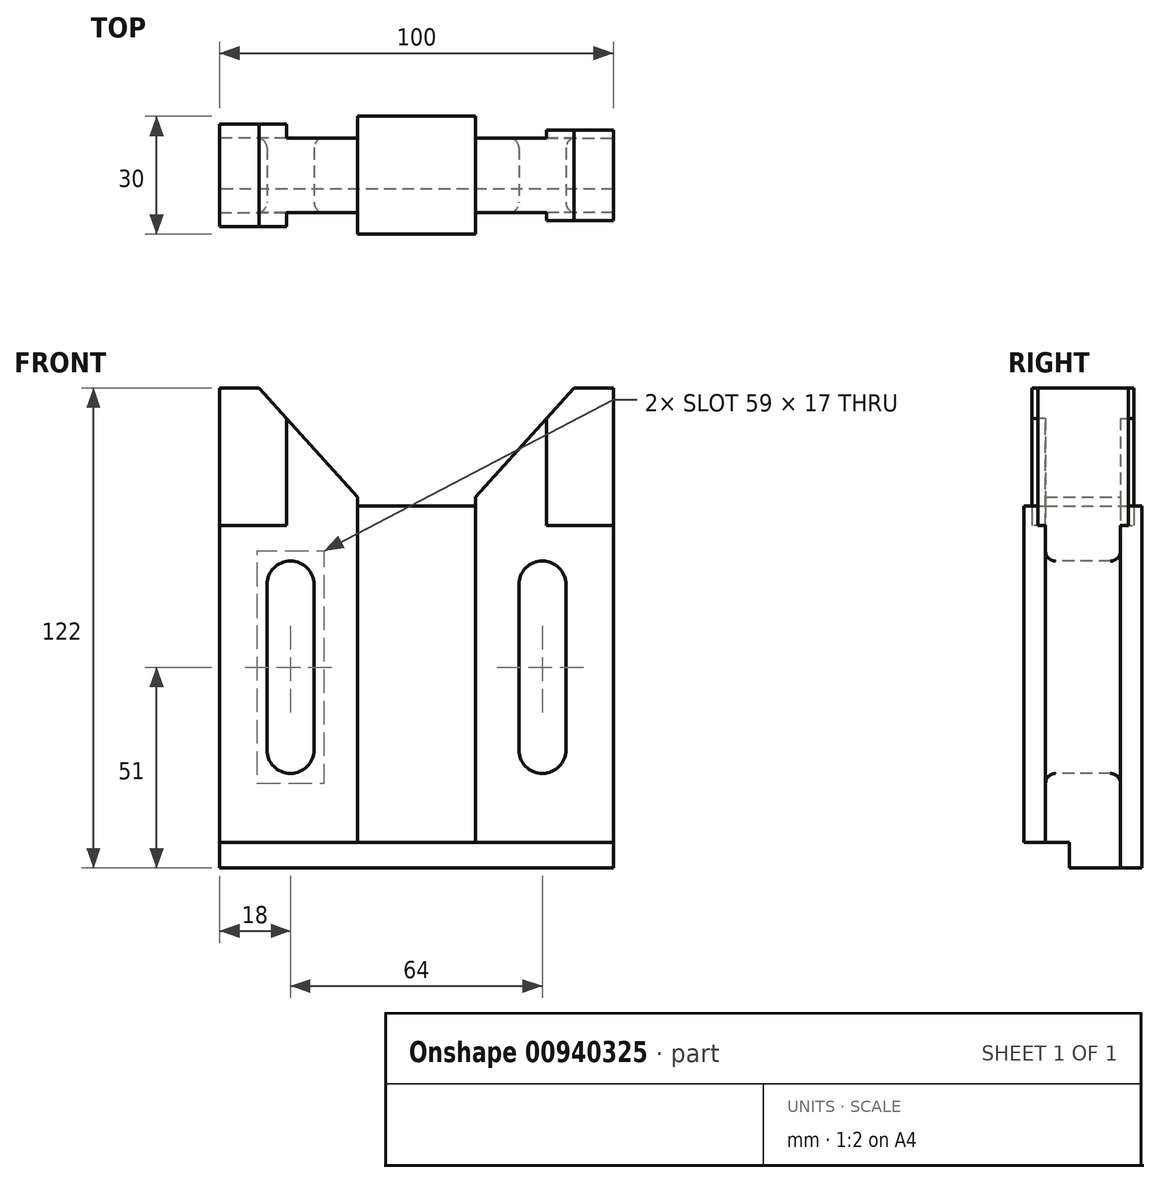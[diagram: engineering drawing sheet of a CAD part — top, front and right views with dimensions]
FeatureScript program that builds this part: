
annotation { "Feature Type Name" : "Feature", "Feature Type Description" : "" }
export const myFeature = defineFeature(function(context is Context, id is Id, definition is map)
    precondition{}
    {
        {
            var Q0;
            Q0=qCreatedBy(makeId("Front.planeOp"),FACE);
            var sketch = newSketch(context, id + "F0", { "sketchPlane" : qUnion([Q0])});
            skLineSegment(sketch, "E0", {"start": v(0, 0) * mm, "end": v(0, 122) * mm});
            skLineSegment(sketch, "E1", {"start": v(0, 122) * mm, "end": v(10, 122) * mm});
            skLineSegment(sketch, "E2", {"start": v(10, 122) * mm, "end": v(35, 94.23) * mm});
            skLineSegment(sketch, "E3", {"start": v(35, 94.23) * mm, "end": v(35, 92) * mm});
            skLineSegment(sketch, "E4.MirrorCS", {"start": v(100, 0) * mm, "end": v(100, 122) * mm});
            skLineSegment(sketch, "E5.MirrorCS", {"start": v(100, 122) * mm, "end": v(90, 122) * mm});
            skLineSegment(sketch, "E6.MirrorCS", {"start": v(90, 122) * mm, "end": v(65, 94.23) * mm});
            skLineSegment(sketch, "E7.MirrorCS", {"start": v(65, 94.23) * mm, "end": v(65, 92) * mm});
            skLineSegment(sketch, "E8", {"start": v(65, 92) * mm, "end": v(35, 92) * mm});
            skLineSegment(sketch, "E9", {"start": v(100, 0) * mm, "end": v(0, 0) * mm});
            skSolve(sketch);
        }
        {
            var Q0;
            Q0=makeQuery(id+"F0.imprint","IMPRINT",FACE,{"disambiguationData":[TD([[makeQuery(id+"F0.imprint","IMPRINT",EDGE,{"derivedFrom":sQuery(id+"F0.wireOp",EDGE,"E0")}),-1.0]])]});
            extrude(context, id + "F1", {"entities" : qUnion([Q0]), "endBound" : BoundingType.SYMMETRIC, "depth" : 30 * mm, "offsetDistance" : 25 * mm});
        }
        {
            var Q0;
            Q0=makeQuery(id+"F1.opExtrude","CAP_FACE",FACE,{"disambiguationData":[OSD([sQuery(id+"F0.wireOp",EDGE,"E0"),sQuery(id+"F0.wireOp",EDGE,"E1"),sQuery(id+"F0.wireOp",EDGE,"E2"),sQuery(id+"F0.wireOp",EDGE,"E3"),sQuery(id+"F0.wireOp",EDGE,"G24MnbEI-lyyA-cKZ0-Hbpa-IpZBKRHigDxM"),sQuery(id+"F0.wireOp",EDGE,"meEAyoxq-4XjU-1zWo-gL1l-UMhUIfnzBa3j"),sQuery(id+"F0.wireOp",EDGE,"10f1b798-4a89-4d97-96c8-caf957162e940.MirrorCS"),sQuery(id+"F0.wireOp",EDGE,"E4.MirrorCS"),sQuery(id+"F0.wireOp",EDGE,"E5.MirrorCS"),sQuery(id+"F0.wireOp",EDGE,"E6.MirrorCS"),sQuery(id+"F0.wireOp",EDGE,"E7.MirrorCS"),sQuery(id+"F0.wireOp",EDGE,"0b4ddf41-7d07-4606-88be-b5c8e99f83050.MirrorCS")])],"isStart":false});
            var sketch = newSketch(context, id + "F2", { "sketchPlane" : qUnion([Q0])});
            skLineSegment(sketch, "E10", {"start": v(50, 128.08) * mm, "end": v(50, -22.5) * mm, "construction": true});
            skPoint(sketch, "E10.startSnap0", {"position": v(50, 100) * mm});
            skSolve(sketch);
        }
        {
            var Q0;
            Q0=makeQuery(id+"F1.opExtrude","SWEPT_FACE",FACE,{"disambiguationData":[OSD([sQuery(id+"F0.wireOp",EDGE,"E0")])]});
            var sketch = newSketch(context, id + "F3", { "sketchPlane" : qUnion([Q0])});
            skLineSegment(sketch, "E11", {"start": v(0, 134.6) * mm, "end": v(0, -10.67) * mm, "construction": true});
            skPoint(sketch, "E11.startSnap0", {"position": v(0, 122) * mm});
            skLineSegment(sketch, "E12", {"start": v(15, 87) * mm, "end": v(11.5, 87) * mm});
            skLineSegment(sketch, "E13", {"start": v(11.5, 87) * mm, "end": v(11.5, 122) * mm});
            skLineSegment(sketch, "E14.MirrorCS", {"start": v(-11.5, 87) * mm, "end": v(-11.5, 122) * mm});
            skLineSegment(sketch, "E15.MirrorCS", {"start": v(-15, 87) * mm, "end": v(-11.5, 87) * mm});
            skLineSegment(sketch, "E16", {"start": v(15, 6.5) * mm, "end": v(3.5, 6.5) * mm});
            skLineSegment(sketch, "E17", {"start": v(3.5, 6.5) * mm, "end": v(3.5, 0) * mm});
            skSolve(sketch);
        }
        {
            var Q0;
            {var subQ0=sQuery(id+"F3.wireOp",EDGE,"E16");Q0=makeQuery(id+"F3.imprint","IMPRINT",FACE,{"disambiguationData":[TD([[makeQuery(id+"F3.imprint","IMPRINT",EDGE,{"derivedFrom":subQ0}),1.0]])]});}
            extrude(context, id + "F4", {"entities" : qUnion([Q0]), "operationType" : NewBodyOperationType.REMOVE, "oppositeDirection" : true, "depth" : 100 * mm, "offsetDistance" : 25 * mm});
        }
        {
            var Q0;
            Q0=makeQuery(id+"F2.imprint","IMPRINT",FACE,{"disambiguationData":[TD([[makeQuery(id+"F2.imprint","IMPRINT",EDGE,{"derivedFrom":makeQuery(id+"F1.opExtrude","CAP_EDGE",EDGE,{"disambiguationData":[OSD([sQuery(id+"F0.wireOp",EDGE,"E0")])],"isStart":false})}),-1.0]])]});
            var sketch = newSketch(context, id + "F5", { "sketchPlane" : qUnion([Q0])});
            skLineSegment(sketch, "E18", {"start": v(0, 87) * mm, "end": v(17, 87) * mm});
            skLineSegment(sketch, "E19", {"start": v(17, 87) * mm, "end": v(17, 114.23) * mm});
            skLineSegment(sketch, "E20", {"start": v(17, 114.23) * mm, "end": v(35, 94.23) * mm});
            skLineSegment(sketch, "E21", {"start": v(35, 94.23) * mm, "end": v(35, 94.23) * mm});
            skLineSegment(sketch, "E22", {"start": v(35, 94.23) * mm, "end": v(35, 6.5) * mm});
            skLineSegment(sketch, "E23", {"start": v(35, 6.5) * mm, "end": v(0, 6.5) * mm});
            skLineSegment(sketch, "E24", {"start": v(0, 6.5) * mm, "end": v(0, 87) * mm});
            skLineSegment(sketch, "E25.MirrorCS", {"start": v(65, 94.23) * mm, "end": v(65, 6.5) * mm});
            skLineSegment(sketch, "E26.MirrorCS", {"start": v(65, 94.23) * mm, "end": v(65, 94.23) * mm});
            skLineSegment(sketch, "E27.MirrorCS", {"start": v(83, 114.23) * mm, "end": v(65, 94.23) * mm});
            skLineSegment(sketch, "E28.MirrorCS", {"start": v(83, 87) * mm, "end": v(83, 114.23) * mm});
            skLineSegment(sketch, "E29.MirrorCS", {"start": v(100, 87) * mm, "end": v(83, 87) * mm});
            skLineSegment(sketch, "E30.MirrorCS", {"start": v(100, 6.5) * mm, "end": v(100, 87) * mm});
            skLineSegment(sketch, "E31.MirrorCS", {"start": v(65, 6.5) * mm, "end": v(100, 6.5) * mm});
            skSolve(sketch);
        }
        {
            var Q0;
            Q0=makeQuery(id+"F5.imprint","IMPRINT",FACE,{"disambiguationData":[TD([[makeQuery(id+"F5.imprint","IMPRINT",EDGE,{"derivedFrom":sQuery(id+"F5.wireOp",EDGE,"E18")}),-1.0]])]});
            var Q1;
            Q1=makeQuery(id+"F5.imprint","IMPRINT",FACE,{"disambiguationData":[TD([[makeQuery(id+"F5.imprint","IMPRINT",EDGE,{"derivedFrom":sQuery(id+"F5.wireOp",EDGE,"E25.MirrorCS")}),1.0]])]});
            extrude(context, id + "F6", {"entities" : qUnion([Q0, Q1]), "operationType" : NewBodyOperationType.REMOVE, "oppositeDirection" : true, "depth" : 5.5 * mm, "offsetDistance" : 25 * mm});
        }
        {
            var Q0;
            Q0=makeQuery(id+"F2.imprint","IMPRINT",FACE,{"disambiguationData":[TD([[makeQuery(id+"F2.imprint","IMPRINT",EDGE,{"derivedFrom":makeQuery(id+"F1.opExtrude","CAP_EDGE",EDGE,{"disambiguationData":[OSD([sQuery(id+"F0.wireOp",EDGE,"E0")])],"isStart":false})}),-1.0]])]});
            var sketch = newSketch(context, id + "F7", { "sketchPlane" : qUnion([Q0])});
            skLineSegment(sketch, "E32", {"start": v(90, 122) * mm, "end": v(100, 122) * mm});
            skLineSegment(sketch, "E33", {"start": v(100, 122) * mm, "end": v(100, 87) * mm});
            skLineSegment(sketch, "E34", {"start": v(100, 87) * mm, "end": v(83, 87) * mm});
            skLineSegment(sketch, "E35", {"start": v(83, 87) * mm, "end": v(83, 114.23) * mm});
            skLineSegment(sketch, "E36", {"start": v(83, 114.23) * mm, "end": v(90, 122) * mm});
            skSolve(sketch);
        }
        {
            var Q0;
            Q0=makeQuery(id+"F7.imprint","IMPRINT",FACE,{"disambiguationData":[TD([[makeQuery(id+"F7.imprint","IMPRINT",EDGE,{"derivedFrom":sQuery(id+"F7.wireOp",EDGE,"E32")}),1.0]])]});
            extrude(context, id + "F8", {"entities" : qUnion([Q0]), "operationType" : NewBodyOperationType.REMOVE, "oppositeDirection" : true, "depth" : 3.5 * mm, "offsetDistance" : 25 * mm});
        }
        {
            var Q0;
            Q0=makeQuery(id+"F1.opExtrude","CAP_FACE",FACE,{"disambiguationData":[OSD([sQuery(id+"F0.wireOp",EDGE,"E0"),sQuery(id+"F0.wireOp",EDGE,"E1"),sQuery(id+"F0.wireOp",EDGE,"E2"),sQuery(id+"F0.wireOp",EDGE,"E3"),sQuery(id+"F0.wireOp",EDGE,"G24MnbEI-lyyA-cKZ0-Hbpa-IpZBKRHigDxM"),sQuery(id+"F0.wireOp",EDGE,"meEAyoxq-4XjU-1zWo-gL1l-UMhUIfnzBa3j"),sQuery(id+"F0.wireOp",EDGE,"10f1b798-4a89-4d97-96c8-caf957162e940.MirrorCS"),sQuery(id+"F0.wireOp",EDGE,"E4.MirrorCS"),sQuery(id+"F0.wireOp",EDGE,"E5.MirrorCS"),sQuery(id+"F0.wireOp",EDGE,"E6.MirrorCS"),sQuery(id+"F0.wireOp",EDGE,"E7.MirrorCS"),sQuery(id+"F0.wireOp",EDGE,"0b4ddf41-7d07-4606-88be-b5c8e99f83050.MirrorCS")])],"isStart":true});
            var sketch = newSketch(context, id + "F9", { "sketchPlane" : qUnion([Q0])});
            skLineSegment(sketch, "E37", {"start": v(-50, 127.91) * mm, "end": v(-50, -24.03) * mm, "construction": true});
            skLineSegment(sketch, "E38", {"start": v(-17, 114.23) * mm, "end": v(-17, 87) * mm});
            skLineSegment(sketch, "E39", {"start": v(-17, 87) * mm, "end": v(0, 87) * mm});
            skLineSegment(sketch, "E40", {"start": v(-17, 114.23) * mm, "end": v(-35, 94.23) * mm});
            skLineSegment(sketch, "E41", {"start": v(-35, 94.23) * mm, "end": v(-35, 94.23) * mm});
            skLineSegment(sketch, "E42", {"start": v(-35, 94.23) * mm, "end": v(-50, 94.23) * mm});
            skLineSegment(sketch, "E43", {"start": v(-50, 94.23) * mm, "end": v(-50, 0) * mm});
            skLineSegment(sketch, "E44", {"start": v(-50, 0) * mm, "end": v(0, 0) * mm});
            skLineSegment(sketch, "E45", {"start": v(0, 0) * mm, "end": v(0, 87) * mm});
            skLineSegment(sketch, "E46", {"start": v(-17, 87) * mm, "end": v(-17, 114.23) * mm});
            skLineSegment(sketch, "E47.MirrorCS", {"start": v(-65, 94.23) * mm, "end": v(-50, 94.23) * mm});
            skLineSegment(sketch, "E48.MirrorCS", {"start": v(-65, 94.23) * mm, "end": v(-65, 94.23) * mm});
            skLineSegment(sketch, "E49.MirrorCS", {"start": v(-83, 114.23) * mm, "end": v(-65, 94.23) * mm});
            skLineSegment(sketch, "E50.MirrorCS", {"start": v(-83, 114.23) * mm, "end": v(-83, 87) * mm});
            skLineSegment(sketch, "E51.MirrorCS", {"start": v(-83, 87) * mm, "end": v(-100, 87) * mm});
            skLineSegment(sketch, "E52.MirrorCS", {"start": v(-100, 0) * mm, "end": v(-100, 87) * mm});
            skLineSegment(sketch, "E53.MirrorCS", {"start": v(-50, 0) * mm, "end": v(-100, 0) * mm});
            skLineSegment(sketch, "E54", {"start": v(-35, 94.23) * mm, "end": v(-35, 0) * mm});
            skLineSegment(sketch, "E55.MirrorCS", {"start": v(-65, 94.23) * mm, "end": v(-65, 0) * mm});
            skSolve(sketch);
        }
        {
            var Q0;
            Q0=makeQuery(id+"F9.imprint","IMPRINT",FACE,{"disambiguationData":[TD([[makeQuery(id+"F9.imprint","IMPRINT",EDGE,{"derivedFrom":sQuery(id+"F9.wireOp",EDGE,"E39")}),-1.0]])]});
            var Q1;
            {var subQ0=sQuery(id+"F9.wireOp",EDGE,"E55.MirrorCS");Q1=makeQuery(id+"F9.imprint","IMPRINT",FACE,{"disambiguationData":[TD([[makeQuery(id+"F9.imprint","IMPRINT",EDGE,{"derivedFrom":subQ0}),-1.0]])]});}
            extrude(context, id + "F10", {"entities" : qUnion([Q0, Q1]), "operationType" : NewBodyOperationType.REMOVE, "oppositeDirection" : true, "depth" : 5.5 * mm, "offsetDistance" : 25 * mm});
        }
        {
            var Q0;
            {var subQ0=sQuery(id+"F0.wireOp",EDGE,"E6.MirrorCS");var subQ1=sQuery(id+"F0.wireOp",EDGE,"E5.MirrorCS");var subQ2=sQuery(id+"F0.wireOp",EDGE,"E4.MirrorCS");Q0=makeQuery(id+"F10.boolean.opBoolean","SPLIT",FACE,{"disambiguationData":[TD([makeQuery(id+"F1.opExtrude","SWEPT_FACE",FACE,{"disambiguationData":[OSD([subQ2])]})])],"derivedFrom":makeQuery(id+"F1.opExtrude","CAP_FACE",FACE,{"disambiguationData":[OSD([sQuery(id+"F0.wireOp",EDGE,"E0"),sQuery(id+"F0.wireOp",EDGE,"E1"),sQuery(id+"F0.wireOp",EDGE,"E2"),sQuery(id+"F0.wireOp",EDGE,"E3"),sQuery(id+"F0.wireOp",EDGE,"G24MnbEI-lyyA-cKZ0-Hbpa-IpZBKRHigDxM"),sQuery(id+"F0.wireOp",EDGE,"meEAyoxq-4XjU-1zWo-gL1l-UMhUIfnzBa3j"),sQuery(id+"F0.wireOp",EDGE,"10f1b798-4a89-4d97-96c8-caf957162e940.MirrorCS"),subQ2,subQ1,subQ0,sQuery(id+"F0.wireOp",EDGE,"E7.MirrorCS"),sQuery(id+"F0.wireOp",EDGE,"0b4ddf41-7d07-4606-88be-b5c8e99f83050.MirrorCS")])],"isStart":true})});}
            var sketch = newSketch(context, id + "F11", { "sketchPlane" : qUnion([Q0])});
            skLineSegment(sketch, "E56", {"start": v(-100, 122) * mm, "end": v(-90, 122) * mm});
            skLineSegment(sketch, "E57", {"start": v(-90, 122) * mm, "end": v(-83, 114.23) * mm});
            skLineSegment(sketch, "E58", {"start": v(-83, 114.23) * mm, "end": v(-83, 87) * mm});
            skLineSegment(sketch, "E59", {"start": v(-83, 87) * mm, "end": v(-100, 87) * mm});
            skLineSegment(sketch, "E60", {"start": v(-100, 87) * mm, "end": v(-100, 122) * mm});
            skSolve(sketch);
        }
        {
            var Q0;
            Q0=makeQuery(id+"F11.imprint","IMPRINT",FACE,{"disambiguationData":[TD([[makeQuery(id+"F11.imprint","IMPRINT",EDGE,{"derivedFrom":sQuery(id+"F11.wireOp",EDGE,"E56")}),-1.0]])]});
            extrude(context, id + "F12", {"entities" : qUnion([Q0]), "operationType" : NewBodyOperationType.REMOVE, "oppositeDirection" : true, "depth" : 3.5 * mm, "offsetDistance" : 25 * mm});
        }
        {
            var Q0;
            Q0=makeQuery(id+"F2.imprint","IMPRINT",FACE,{"disambiguationData":[TD([[makeQuery(id+"F2.imprint","IMPRINT",EDGE,{"derivedFrom":makeQuery(id+"F1.opExtrude","CAP_EDGE",EDGE,{"disambiguationData":[OSD([sQuery(id+"F0.wireOp",EDGE,"E0")])],"isStart":false})}),-1.0]])]});
            var sketch = newSketch(context, id + "F13", { "sketchPlane" : qUnion([Q0])});
            skArc(sketch, "E61", {"start": v(24, 72) * mm, "mid": v(18, 78) * mm, "end": v(12, 72) * mm});
            skArc(sketch, "E62", {"start": v(12, 30) * mm, "mid": v(18, 24) * mm, "end": v(24, 30) * mm});
            skLineSegment(sketch, "E63", {"start": v(12, 72) * mm, "end": v(12, 30) * mm});
            skLineSegment(sketch, "E64", {"start": v(24, 72) * mm, "end": v(24, 30) * mm});
            skLineSegment(sketch, "E65.MirrorCS", {"start": v(76, 72) * mm, "end": v(76, 30) * mm});
            skArc(sketch, "E66.MirrorCS", {"start": v(76, 72) * mm, "mid": v(82, 78) * mm, "end": v(88, 72) * mm});
            skLineSegment(sketch, "E67.MirrorCS", {"start": v(88, 72) * mm, "end": v(88, 30) * mm});
            skArc(sketch, "E68.MirrorCS", {"start": v(88, 30) * mm, "mid": v(82, 24) * mm, "end": v(76, 30) * mm});
            skSolve(sketch);
        }
        {
            var Q0;
            Q0 = qSketchRegion(id + "F13", true);
            extrude(context, id + "F14", {"entities" : qUnion([Q0]), "operationType" : NewBodyOperationType.REMOVE, "oppositeDirection" : true, "depth" : 25 * mm, "offsetDistance" : 25 * mm});
        }
        {
            var Q0;
            Q0=makeQuery(id+"F14.boolean.opBoolean","INTERSECT",EDGE,{"derivedFrom":[makeQuery(id+"F10.boolean.opBoolean","COPY",FACE,{"derivedFrom":makeQuery(id+"F10.opExtrude","CAP_FACE",FACE,{"disambiguationData":[OSD([sQuery(id+"F9.wireOp",EDGE,"E55.MirrorCS"),sQuery(id+"F9.wireOp",EDGE,"E48.MirrorCS"),sQuery(id+"F9.wireOp",EDGE,"E49.MirrorCS"),sQuery(id+"F9.wireOp",EDGE,"E50.MirrorCS"),sQuery(id+"F9.wireOp",EDGE,"E51.MirrorCS"),sQuery(id+"F9.wireOp",EDGE,"E52.MirrorCS"),sQuery(id+"F9.wireOp",EDGE,"E53.MirrorCS")])],"isStart":false})}),makeQuery(id+"F14.opExtrude","SWEPT_FACE",FACE,{"disambiguationData":[OSD([sQuery(id+"F13.wireOp",EDGE,"E65.MirrorCS")])]})]});
            var Q1;
            Q1=makeQuery(id+"F14.boolean.opBoolean","INTERSECT",EDGE,{"derivedFrom":[makeQuery(id+"F10.boolean.opBoolean","COPY",FACE,{"derivedFrom":makeQuery(id+"F10.opExtrude","CAP_FACE",FACE,{"disambiguationData":[OSD([sQuery(id+"F9.wireOp",EDGE,"E39"),sQuery(id+"F9.wireOp",EDGE,"E40"),sQuery(id+"F9.wireOp",EDGE,"E41"),sQuery(id+"F9.wireOp",EDGE,"E44"),sQuery(id+"F9.wireOp",EDGE,"E45"),sQuery(id+"F9.wireOp",EDGE,"E46"),sQuery(id+"F9.wireOp",EDGE,"E54")])],"isStart":false})}),makeQuery(id+"F14.opExtrude","SWEPT_FACE",FACE,{"disambiguationData":[OSD([sQuery(id+"F13.wireOp",EDGE,"E64")])]})]});
            var Q2;
            Q2=makeQuery(id+"F14.boolean.opBoolean","INTERSECT",EDGE,{"derivedFrom":[makeQuery(id+"F6.boolean.opBoolean","COPY",FACE,{"derivedFrom":makeQuery(id+"F6.opExtrude","CAP_FACE",FACE,{"disambiguationData":[OSD([sQuery(id+"F5.wireOp",EDGE,"E18"),sQuery(id+"F5.wireOp",EDGE,"E19"),sQuery(id+"F5.wireOp",EDGE,"E20"),sQuery(id+"F5.wireOp",EDGE,"E21"),sQuery(id+"F5.wireOp",EDGE,"E22"),sQuery(id+"F5.wireOp",EDGE,"E23"),sQuery(id+"F5.wireOp",EDGE,"E24")])],"isStart":false})}),makeQuery(id+"F14.opExtrude","SWEPT_FACE",FACE,{"disambiguationData":[OSD([sQuery(id+"F13.wireOp",EDGE,"E63")])]})]});
            var Q3;
            Q3=makeQuery(id+"F14.boolean.opBoolean","INTERSECT",EDGE,{"derivedFrom":[makeQuery(id+"F6.boolean.opBoolean","COPY",FACE,{"derivedFrom":makeQuery(id+"F6.opExtrude","CAP_FACE",FACE,{"disambiguationData":[OSD([sQuery(id+"F5.wireOp",EDGE,"E25.MirrorCS"),sQuery(id+"F5.wireOp",EDGE,"E26.MirrorCS"),sQuery(id+"F5.wireOp",EDGE,"E27.MirrorCS"),sQuery(id+"F5.wireOp",EDGE,"E28.MirrorCS"),sQuery(id+"F5.wireOp",EDGE,"E29.MirrorCS"),sQuery(id+"F5.wireOp",EDGE,"E30.MirrorCS"),sQuery(id+"F5.wireOp",EDGE,"E31.MirrorCS")])],"isStart":false})}),makeQuery(id+"F14.opExtrude","SWEPT_FACE",FACE,{"disambiguationData":[OSD([sQuery(id+"F13.wireOp",EDGE,"E65.MirrorCS")])]})]});
            fillet(context, id + "F15", {"entities" : qUnion([Q0, Q1, Q2, Q3]), "radius" : 2.5 * mm, "tangentPropagation" : true, "allowEdgeOverflow" : false});
        }
        {
            var Q0;
            Q0=makeQuery(id+"F1.opExtrude","SWEPT_FACE",FACE,{"disambiguationData":[OSD([sQuery(id+"F0.wireOp",EDGE,"E0")])]});
            var sketch = newSketch(context, id + "F16", { "sketchPlane" : qUnion([Q0])});
            skLineSegment(sketch, "E69", {"start": v(0, 133.84) * mm, "end": v(0, -11.75) * mm, "construction": true});
            skPoint(sketch, "E69.startSnap0", {"position": v(0, 122) * mm});
            skLineSegment(sketch, "E70.bottom", {"start": v(13, 122) * mm, "end": v(35.6, 122) * mm});
            skLineSegment(sketch, "E70.top", {"start": v(13, 87) * mm, "end": v(35.6, 87) * mm});
            skLineSegment(sketch, "E70.left", {"start": v(13, 122) * mm, "end": v(13, 87) * mm});
            skLineSegment(sketch, "E70.right", {"start": v(35.6, 122) * mm, "end": v(35.6, 87) * mm});
            skLineSegment(sketch, "E71.MirrorCS", {"start": v(-13, 122) * mm, "end": v(-13, 87) * mm});
            skLineSegment(sketch, "E72.MirrorCS", {"start": v(-13, 87) * mm, "end": v(-35.6, 87) * mm});
            skLineSegment(sketch, "E73.MirrorCS", {"start": v(-35.6, 122) * mm, "end": v(-35.6, 87) * mm});
            skLineSegment(sketch, "E74.MirrorCS", {"start": v(-13, 122) * mm, "end": v(-35.6, 122) * mm});
            skSolve(sketch);
        }
        {
            var Q0;
            {var subQ2=sQuery(id+"F16.wireOp",EDGE,"E73.MirrorCS");Q0=makeQuery(id+"F16.imprint","IMPRINT",FACE,{"disambiguationData":[TD([[makeQuery(id+"F16.imprint","IMPRINT",EDGE,{"derivedFrom":subQ2}),1.0]])]});}
            var Q1;
            {var subQ2=sQuery(id+"F16.wireOp",EDGE,"E70.right");Q1=makeQuery(id+"F16.imprint","IMPRINT",FACE,{"disambiguationData":[TD([[makeQuery(id+"F16.imprint","IMPRINT",EDGE,{"derivedFrom":subQ2}),-1.0]])]});}
            var Q2;
            {var subQ0=sQuery(id+"F16.wireOp",EDGE,"E71.MirrorCS");Q2=makeQuery(id+"F16.imprint","IMPRINT",FACE,{"disambiguationData":[TD([[makeQuery(id+"F16.imprint","IMPRINT",EDGE,{"derivedFrom":subQ0}),-1.0]])]});}
            var Q3;
            {var subQ3=sQuery(id+"F16.wireOp",EDGE,"E70.left");Q3=makeQuery(id+"F16.imprint","IMPRINT",FACE,{"disambiguationData":[TD([[makeQuery(id+"F16.imprint","IMPRINT",EDGE,{"derivedFrom":subQ3}),1.0]])]});}
            extrude(context, id + "F17", {"entities" : qUnion([Q0, Q1, Q2, Q3]), "operationType" : NewBodyOperationType.REMOVE, "oppositeDirection" : true, "depth" : 17 * mm, "offsetDistance" : 25 * mm});
        }
    });
